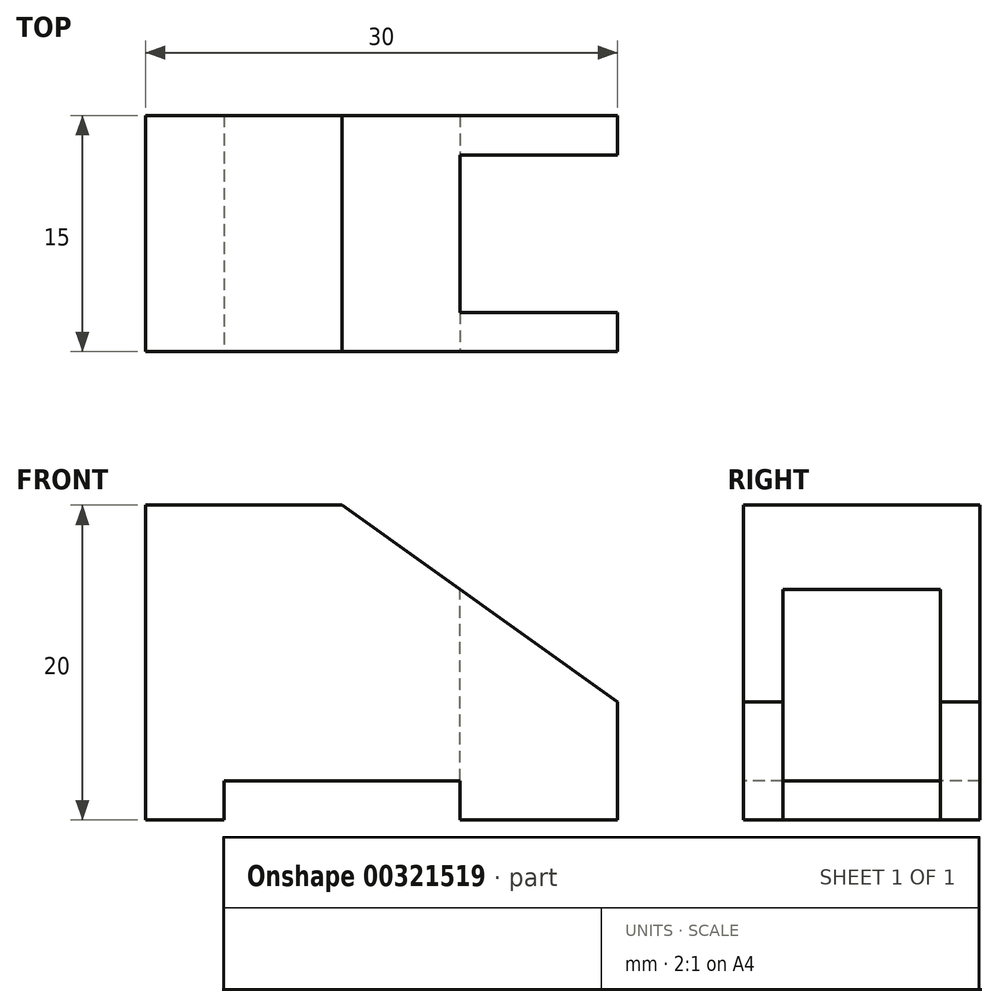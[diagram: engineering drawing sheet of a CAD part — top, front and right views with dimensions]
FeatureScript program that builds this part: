
annotation { "Feature Type Name" : "Feature", "Feature Type Description" : "" }
export const myFeature = defineFeature(function(context is Context, id is Id, definition is map)
    precondition{}
    {
        {
            var Q0;
            Q0=qCreatedBy(makeId("Front.planeOp"),FACE);
            var sketch = newSketch(context, id + "F0", { "sketchPlane" : qUnion([Q0])});
            skLineSegment(sketch, "E0.bottom", {"start": v(0, 0) * mm, "end": v(30, 0) * mm});
            skLineSegment(sketch, "E0.top", {"start": v(0, 20) * mm, "end": v(30, 20) * mm});
            skLineSegment(sketch, "E0.left", {"start": v(0, 0) * mm, "end": v(0, 20) * mm});
            skLineSegment(sketch, "E0.right", {"start": v(30, 0) * mm, "end": v(30, 20) * mm});
            skSolve(sketch);
        }
        {
            var Q0;
            Q0 = qSketchRegion(id + "F0", true);
            extrude(context, id + "F1", {"entities" : qUnion([Q0]), "depth" : 15 * mm});
        }
        {
            var Q0;
            Q0=makeQuery(id+"F1.opExtrude","CAP_FACE",FACE,{"disambiguationData":[OSD([sQuery(id+"F0.wireOp",EDGE,"E0.bottom"),sQuery(id+"F0.wireOp",EDGE,"E0.top"),sQuery(id+"F0.wireOp",EDGE,"E0.left"),sQuery(id+"F0.wireOp",EDGE,"E0.right")])],"isStart":false});
            var sketch = newSketch(context, id + "F2", { "sketchPlane" : qUnion([Q0])});
            skLineSegment(sketch, "E1", {"start": v(30, 20) * mm, "end": v(12.5, 20) * mm});
            skLineSegment(sketch, "E2", {"start": v(30, 20) * mm, "end": v(30, 7.5) * mm});
            skLineSegment(sketch, "E3", {"start": v(30, 7.5) * mm, "end": v(12.5, 20) * mm});
            skSolve(sketch);
        }
        {
            var Q0;
            Q0 = qSketchRegion(id + "F2", true);
            extrude(context, id + "F3", {"entities" : qUnion([Q0]), "operationType" : NewBodyOperationType.REMOVE, "endBound" : BoundingType.THROUGH_ALL, "oppositeDirection" : true, "depth" : 25 * mm});
        }
        {
            var Q0;
            Q0=makeQuery(id+"F1.opExtrude","CAP_FACE",FACE,{"disambiguationData":[OSD([sQuery(id+"F0.wireOp",EDGE,"E0.bottom"),sQuery(id+"F0.wireOp",EDGE,"E0.top"),sQuery(id+"F0.wireOp",EDGE,"E0.left"),sQuery(id+"F0.wireOp",EDGE,"E0.right")])],"isStart":false});
            var sketch = newSketch(context, id + "F4", { "sketchPlane" : qUnion([Q0])});
            skLineSegment(sketch, "E4.bottom", {"start": v(5, 0) * mm, "end": v(20, 0) * mm});
            skLineSegment(sketch, "E4.top", {"start": v(5, 2.5) * mm, "end": v(20, 2.5) * mm});
            skLineSegment(sketch, "E4.left", {"start": v(5, 0) * mm, "end": v(5, 2.5) * mm});
            skLineSegment(sketch, "E4.right", {"start": v(20, 0) * mm, "end": v(20, 2.5) * mm});
            skSolve(sketch);
        }
        {
            var Q0;
            Q0 = qSketchRegion(id + "F4", true);
            extrude(context, id + "F5", {"entities" : qUnion([Q0]), "operationType" : NewBodyOperationType.REMOVE, "endBound" : BoundingType.THROUGH_ALL, "oppositeDirection" : true, "depth" : 25 * mm});
        }
        {
            var Q0;
            Q0=makeQuery(id+"F1.opExtrude","SWEPT_FACE",FACE,{"disambiguationData":[OSD([sQuery(id+"F0.wireOp",EDGE,"E0.top")])]});
            var sketch = newSketch(context, id + "F6", { "sketchPlane" : qUnion([Q0])});
            skLineSegment(sketch, "E5.bottom", {"start": v(30, -2.5) * mm, "end": v(20, -2.5) * mm});
            skLineSegment(sketch, "E5.top", {"start": v(30, -12.5) * mm, "end": v(20, -12.5) * mm});
            skLineSegment(sketch, "E5.left", {"start": v(30, -2.5) * mm, "end": v(30, -12.5) * mm});
            skLineSegment(sketch, "E5.right", {"start": v(20, -2.5) * mm, "end": v(20, -12.5) * mm});
            skSolve(sketch);
        }
        {
            var Q0;
            Q0 = qSketchRegion(id + "F6", true);
            extrude(context, id + "F7", {"entities" : qUnion([Q0]), "operationType" : NewBodyOperationType.REMOVE, "endBound" : BoundingType.THROUGH_ALL, "oppositeDirection" : true, "depth" : 25 * mm});
        }
    });
